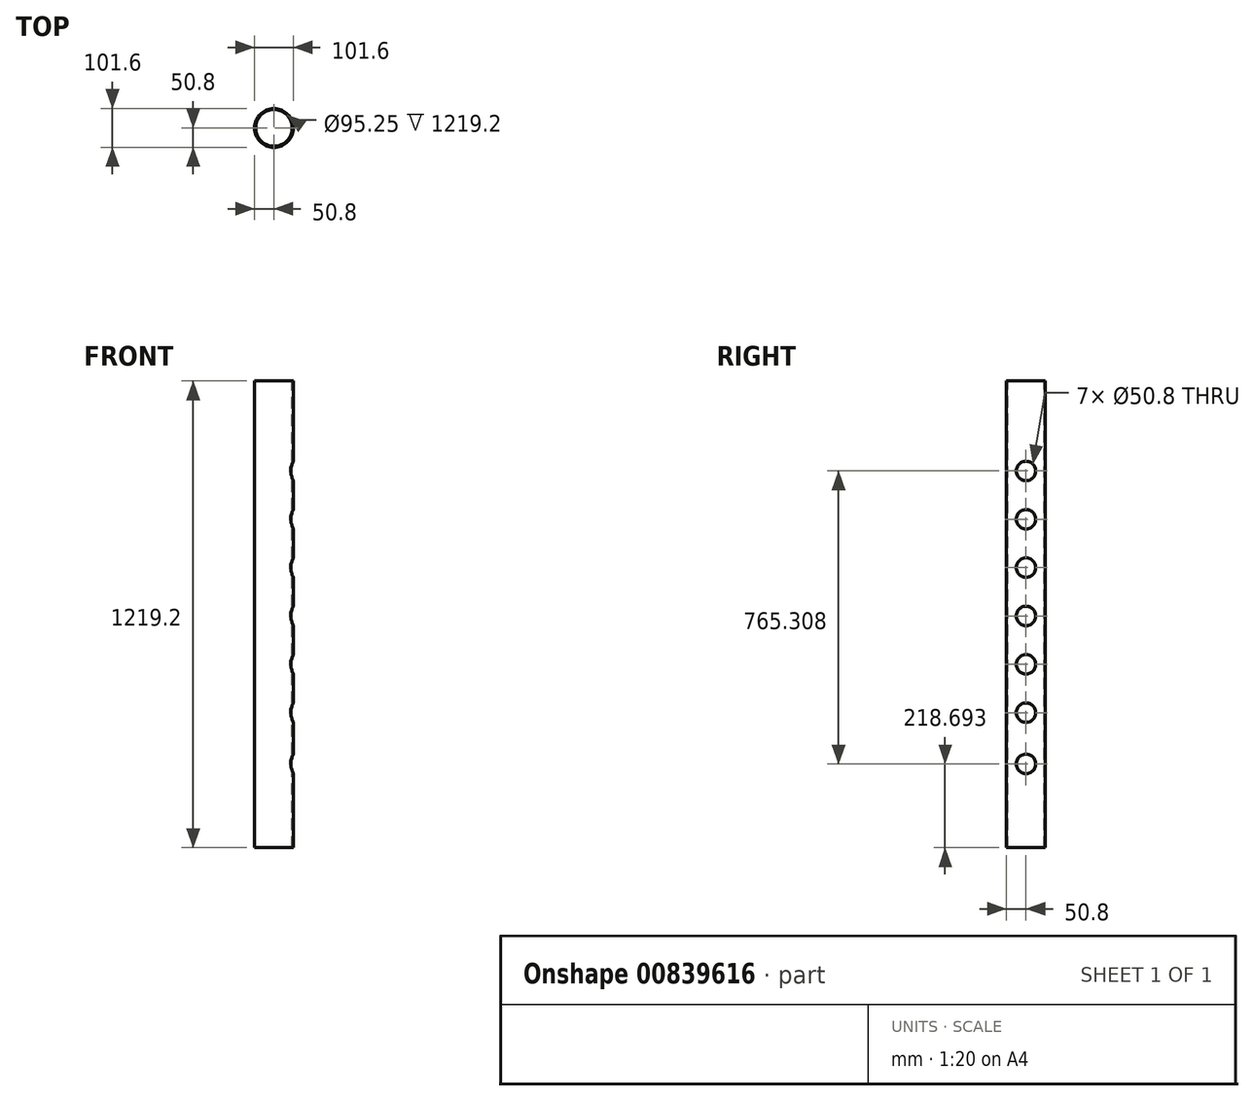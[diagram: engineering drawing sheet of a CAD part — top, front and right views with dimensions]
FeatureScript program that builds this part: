
annotation { "Feature Type Name" : "Feature", "Feature Type Description" : "" }
export const myFeature = defineFeature(function(context is Context, id is Id, definition is map)
    precondition{}
    {
        {
            var Q0;
            Q0=qCreatedBy(makeId("Top.planeOp"),FACE);
            var sketch = newSketch(context, id + "F0", { "sketchPlane" : qUnion([Q0])});
            skCircle(sketch, "E0", {"center": v(0, 0) * mm, "radius": 50.8 * mm});
            skSolve(sketch);
        }
        {
            var Q0;
            Q0 = qSketchRegion(id + "F0", true);
            var Q1;
            Q1=makeQuery(id+"F0.imprint","IMPRINT",FACE,{"disambiguationData":[TD([[makeQuery(id+"F0.imprint","IMPRINT",EDGE,{"derivedFrom":sQuery(id+"F0.wireOp",EDGE,"E0")}),1.0]])]});
            extrude(context, id + "F1", {"entities" : qUnion([Q0, Q1]), "depth" : 1219.2 * mm, "offsetDistance" : 25.4 * mm});
        }
        {
            var Q0;
            Q0=makeQuery(id+"F1.opExtrude","CAP_FACE",FACE,{"disambiguationData":[OSD([sQuery(id+"F0.wireOp",EDGE,"E0")])],"isStart":false});
            var sketch = newSketch(context, id + "F2", { "sketchPlane" : qUnion([Q0])});
            skCircle(sketch, "E1", {"center": v(0, 0) * mm, "radius": 47.63 * mm});
            skSolve(sketch);
        }
        {
            var Q0;
            Q0 = qSketchRegion(id + "F2", true);
            extrude(context, id + "F3", {"entities" : qUnion([Q0]), "operationType" : NewBodyOperationType.REMOVE, "oppositeDirection" : true, "depth" : 1244.6 * mm, "offsetDistance" : 25.4 * mm});
        }
        {
            var Q0;
            Q0=qCreatedBy(makeId("Right.planeOp"),FACE);
            var sketch = newSketch(context, id + "F4", { "sketchPlane" : qUnion([Q0])});
            skCircle(sketch, "E2", {"center": v(0, 984) * mm, "radius": 25.4 * mm});
            skCircle(sketch, "E3", {"center": v(0, 857.7) * mm, "radius": 25.4 * mm});
            skCircle(sketch, "E4", {"center": v(0, 731.4) * mm, "radius": 25.4 * mm});
            skCircle(sketch, "E5", {"center": v(0, 605.09) * mm, "radius": 25.4 * mm});
            skCircle(sketch, "E6", {"center": v(0, 478.78) * mm, "radius": 25.4 * mm});
            skCircle(sketch, "E7", {"center": v(0, 352.47) * mm, "radius": 25.4 * mm});
            skCircle(sketch, "E8", {"center": v(0, 218.7) * mm, "radius": 25.4 * mm});
            skSolve(sketch);
        }
        {
            var Q0;
            Q0 = qSketchRegion(id + "F4", true);
            extrude(context, id + "F5", {"entities" : qUnion([Q0]), "operationType" : NewBodyOperationType.REMOVE, "depth" : 50.8 * mm, "offsetDistance" : 25.4 * mm});
        }
    });
